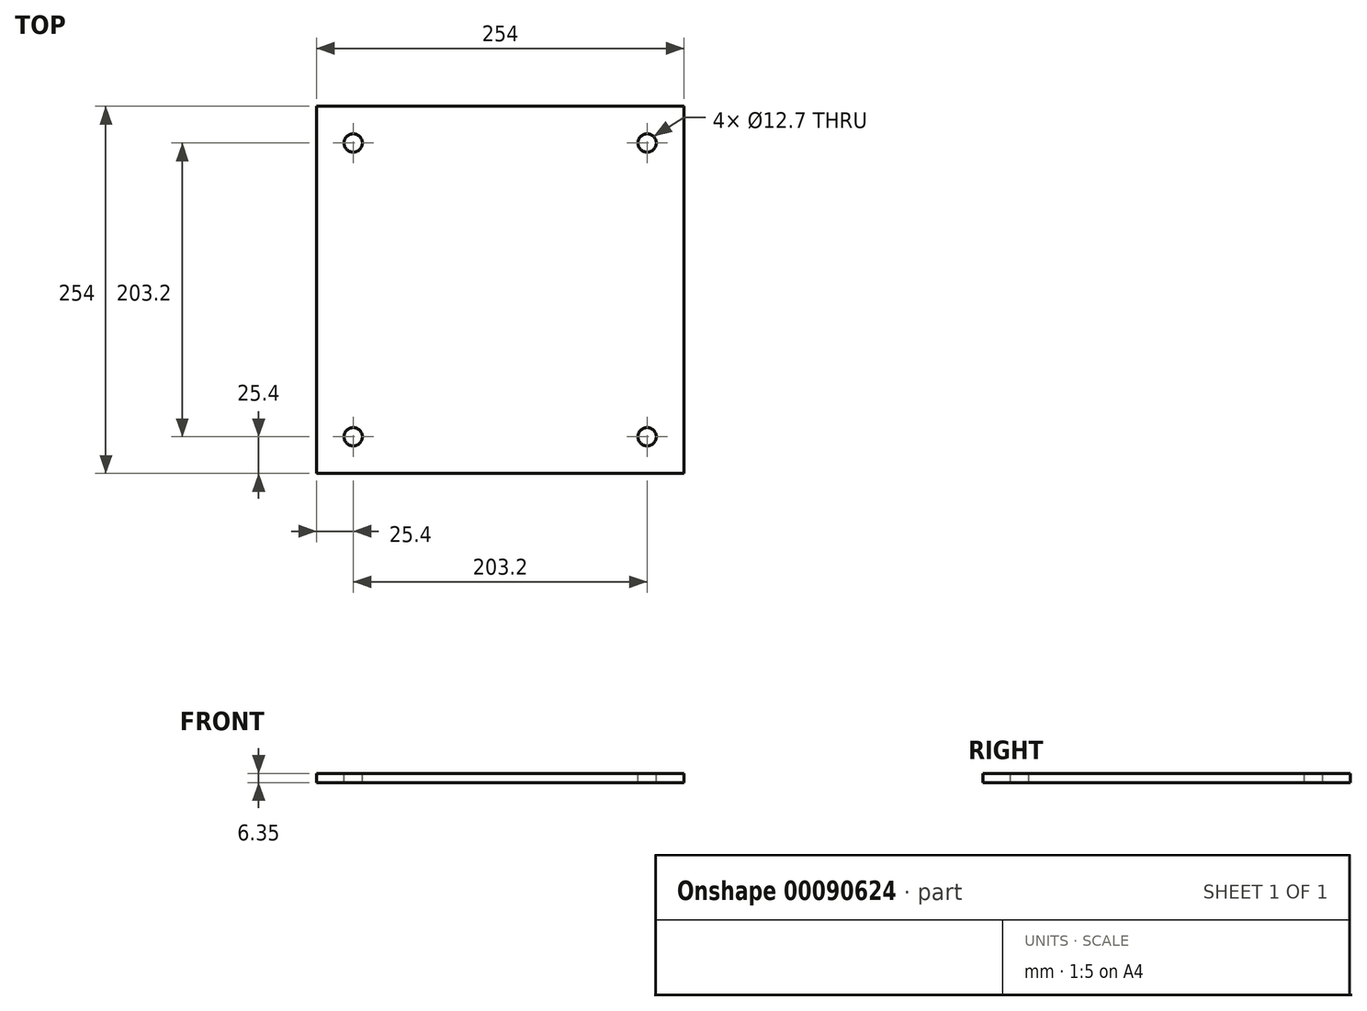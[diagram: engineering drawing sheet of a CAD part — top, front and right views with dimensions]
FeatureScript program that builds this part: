
annotation { "Feature Type Name" : "Feature", "Feature Type Description" : "" }
export const myFeature = defineFeature(function(context is Context, id is Id, definition is map)
    precondition{}
    {
        {
            var Q0;
            Q0=qCreatedBy(makeId("Top.planeOp"),FACE);
            var sketch = newSketch(context, id + "F0", { "sketchPlane" : qUnion([Q0])});
            skLineSegment(sketch, "E0.bottom", {"start": v(127, -127) * mm, "end": v(-127, -127) * mm});
            skLineSegment(sketch, "E0.top", {"start": v(127, 127) * mm, "end": v(-127, 127) * mm});
            skLineSegment(sketch, "E0.left", {"start": v(127, -127) * mm, "end": v(127, 127) * mm});
            skLineSegment(sketch, "E0.right", {"start": v(-127, -127) * mm, "end": v(-127, 127) * mm});
            skPoint(sketch, "E0.middle", {"position": v(0, 0) * mm});
            skSolve(sketch);
        }
        {
            var Q0;
            Q0 = qSketchRegion(id + "F0", true);
            extrude(context, id + "F1", {"entities" : qUnion([Q0]), "depth" : 6.35 * mm});
        }
        {
            var Q0;
            Q0=makeQuery(id+"F1.opExtrude","CAP_FACE",FACE,{"disambiguationData":[OSD([sQuery(id+"F0.wireOp",EDGE,"E0.bottom"),sQuery(id+"F0.wireOp",EDGE,"E0.top"),sQuery(id+"F0.wireOp",EDGE,"E0.left"),sQuery(id+"F0.wireOp",EDGE,"E0.right")])],"isStart":false});
            var sketch = newSketch(context, id + "F2", { "sketchPlane" : qUnion([Q0])});
            skCircle(sketch, "E1", {"center": v(-101.6, 101.6) * mm, "radius": 6.35 * mm});
            skCircle(sketch, "E2.0.1.0", {"center": v(-101.6, -101.6) * mm, "radius": 6.35 * mm});
            skCircle(sketch, "E2.1.0.0", {"center": v(101.6, 101.6) * mm, "radius": 6.35 * mm});
            skCircle(sketch, "E2.1.1.0", {"center": v(101.6, -101.6) * mm, "radius": 6.35 * mm});
            skLineSegment(sketch, "E2.direction1", {"start": v(-101.6, 101.6) * mm, "end": v(101.6, 101.6) * mm, "construction": true});
            skLineSegment(sketch, "E2.direction2", {"start": v(-101.6, 101.6) * mm, "end": v(-101.6, -101.6) * mm, "construction": true});
            skSolve(sketch);
        }
        {
            var Q0;
            Q0 = qSketchRegion(id + "F2", true);
            var Q1;
            {var subQ0=sQuery(id+"F2.wireOp",EDGE,"fcaae9ca-0fe3-4ba5-9361-49e8d2982260.0.left");var subQ5=sQuery(id+"F2.wireOp",EDGE,"fcaae9ca-0fe3-4ba5-9361-49e8d2982260.4.left");var subQ6=makeQuery(id+"F2.imprint","INTERSECT",VERTEX,{"derivedFrom":[subQ0,subQ5]});Q1=makeQuery(id+"F2.imprint","IMPRINT",FACE,{"disambiguationData":[TD([[makeQuery(id+"F2.imprint","IMPRINT",EDGE,{"disambiguationData":[TD([[subQ6,-1.0]])],"derivedFrom":subQ5}),-1.0]])]});}
            var Q2;
            {var subQ0=sQuery(id+"F2.wireOp",EDGE,"fcaae9ca-0fe3-4ba5-9361-49e8d2982260.3.right");var subQ5=sQuery(id+"F2.wireOp",EDGE,"fcaae9ca-0fe3-4ba5-9361-49e8d2982260.5.left");var subQ6=makeQuery(id+"F2.imprint","INTERSECT",VERTEX,{"derivedFrom":[subQ0,subQ5]});Q2=makeQuery(id+"F2.imprint","IMPRINT",FACE,{"disambiguationData":[TD([[makeQuery(id+"F2.imprint","IMPRINT",EDGE,{"disambiguationData":[TD([[subQ6,1.0]])],"derivedFrom":subQ5}),-1.0]])]});}
            var Q3;
            {var subQ3=sQuery(id+"F2.wireOp",EDGE,"fcaae9ca-0fe3-4ba5-9361-49e8d2982260.8.right");var subQ5=sQuery(id+"F2.wireOp",EDGE,"fcaae9ca-0fe3-4ba5-9361-49e8d2982260.0.left");var subQ6=makeQuery(id+"F2.imprint","INTERSECT",VERTEX,{"derivedFrom":[subQ5,subQ3]});Q3=makeQuery(id+"F2.imprint","IMPRINT",FACE,{"disambiguationData":[TD([[makeQuery(id+"F2.imprint","IMPRINT",EDGE,{"disambiguationData":[TD([[subQ6,-1.0]])],"derivedFrom":subQ5}),-1.0]])]});}
            var Q4;
            {var subQ3=sQuery(id+"F2.wireOp",EDGE,"fcaae9ca-0fe3-4ba5-9361-49e8d2982260.8.endCap");var subQ5=sQuery(id+"F2.wireOp",EDGE,"fcaae9ca-0fe3-4ba5-9361-49e8d2982260.6.right");var subQ6=makeQuery(id+"F2.imprint","INTERSECT",VERTEX,{"derivedFrom":[subQ5,subQ3]});Q4=makeQuery(id+"F2.imprint","IMPRINT",FACE,{"disambiguationData":[TD([[makeQuery(id+"F2.imprint","IMPRINT",EDGE,{"disambiguationData":[TD([[subQ6,-1.0]])],"derivedFrom":subQ5}),1.0]])]});}
            var Q5;
            {var subQ0=sQuery(id+"F2.wireOp",EDGE,"fcaae9ca-0fe3-4ba5-9361-49e8d2982260.6.startCap");Q5=makeQuery(id+"F2.imprint","IMPRINT",FACE,{"disambiguationData":[TD([[makeQuery(id+"F2.imprint","IMPRINT",EDGE,{"derivedFrom":subQ0}),1.0]])]});}
            var Q6;
            {var subQ4=sQuery(id+"F2.wireOp",EDGE,"fcaae9ca-0fe3-4ba5-9361-49e8d2982260.6.startCap");Q6=makeQuery(id+"F2.imprint","IMPRINT",FACE,{"disambiguationData":[TD([[makeQuery(id+"F2.imprint","IMPRINT",EDGE,{"derivedFrom":subQ4}),-1.0]])]});}
            var Q7;
            {var subQ0=sQuery(id+"F2.wireOp",EDGE,"fcaae9ca-0fe3-4ba5-9361-49e8d2982260.6.right");var subQ5=sQuery(id+"F2.wireOp",EDGE,"fcaae9ca-0fe3-4ba5-9361-49e8d2982260.3.right");var subQ7=makeQuery(id+"F2.imprint","INTERSECT",VERTEX,{"derivedFrom":[subQ5,subQ0]});Q7=makeQuery(id+"F2.imprint","IMPRINT",FACE,{"disambiguationData":[TD([[makeQuery(id+"F2.imprint","IMPRINT",EDGE,{"disambiguationData":[TD([[subQ7,-1.0]])],"derivedFrom":subQ5}),1.0]])]});}
            var Q8;
            {var subQ0=sQuery(id+"F2.wireOp",EDGE,"eogiIR2U-LT6g-LpLl-vn9w-FLxRaLRIBlY3");var subQ1=sQuery(id+"F2.wireOp",EDGE,"OlrpAAhb-PgXn-HwtC-GuVG-OjTCxttYwNpF");var subQ2=makeQuery(id+"F2.imprint","INTERSECT",VERTEX,{"derivedFrom":[subQ1,subQ0]});Q8=makeQuery(id+"F2.imprint","IMPRINT",FACE,{"disambiguationData":[TD([[makeQuery(id+"F2.imprint","IMPRINT",EDGE,{"disambiguationData":[TD([[subQ2,-1.0]])],"derivedFrom":subQ0}),-1.0]])]});}
            var Q9;
            {var subQ0=sQuery(id+"F2.wireOp",EDGE,"BpUyd5S9-NxuM-rI9K-ceQx-ny6DKXw1QPVt");var subQ1=sQuery(id+"F2.wireOp",EDGE,"OlrpAAhb-PgXn-HwtC-GuVG-OjTCxttYwNpF");var subQ2=makeQuery(id+"F2.imprint","INTERSECT",VERTEX,{"derivedFrom":[subQ1,subQ0]});Q9=makeQuery(id+"F2.imprint","IMPRINT",FACE,{"disambiguationData":[TD([[makeQuery(id+"F2.imprint","IMPRINT",EDGE,{"disambiguationData":[TD([[subQ2,1.0]])],"derivedFrom":subQ1}),1.0]])]});}
            var Q10;
            {var subQ0=sQuery(id+"F2.wireOp",EDGE,"UC7Wnhcp-SDgs-MwhC-QxEK-dL5DjtuIj0PG");var subQ1=sQuery(id+"F2.wireOp",EDGE,"RPupRvv0-u5yY-Xdj7-EinU-e93FE9O1bOhS");var subQ2=makeQuery(id+"F2.imprint","INTERSECT",VERTEX,{"derivedFrom":[subQ1,subQ0]});Q10=makeQuery(id+"F2.imprint","IMPRINT",FACE,{"disambiguationData":[TD([[makeQuery(id+"F2.imprint","IMPRINT",EDGE,{"disambiguationData":[TD([[subQ2,1.0]])],"derivedFrom":subQ1}),-1.0]])]});}
            var Q11;
            {var subQ0=sQuery(id+"F2.wireOp",EDGE,"UC7Wnhcp-SDgs-MwhC-QxEK-dL5DjtuIj0PG");var subQ1=sQuery(id+"F2.wireOp",EDGE,"skyEo2ta-Vul4-0HxA-M2Rf-Yz6B0rTyctfK");var subQ2=makeQuery(id+"F2.imprint","INTERSECT",VERTEX,{"derivedFrom":[subQ1,subQ0]});Q11=makeQuery(id+"F2.imprint","IMPRINT",FACE,{"disambiguationData":[TD([[makeQuery(id+"F2.imprint","IMPRINT",EDGE,{"disambiguationData":[TD([[subQ2,1.0]])],"derivedFrom":subQ0}),-1.0]])]});}
            var Q12;
            {var subQ0=sQuery(id+"F2.wireOp",EDGE,"skyEo2ta-Vul4-0HxA-M2Rf-Yz6B0rTyctfK");var subQ1=sQuery(id+"F2.wireOp",EDGE,"BpUyd5S9-NxuM-rI9K-ceQx-ny6DKXw1QPVt");var subQ2=makeQuery(id+"F2.imprint","INTERSECT",VERTEX,{"derivedFrom":[subQ1,subQ0]});Q12=makeQuery(id+"F2.imprint","IMPRINT",FACE,{"disambiguationData":[TD([[makeQuery(id+"F2.imprint","IMPRINT",EDGE,{"disambiguationData":[TD([[subQ2,1.0]])],"derivedFrom":subQ1}),1.0]])]});}
            extrude(context, id + "F3", {"entities" : qUnion([Q0, Q1, Q2, Q3, Q4, Q5, Q6, Q7, Q8, Q9, Q10, Q11, Q12]), "operationType" : NewBodyOperationType.REMOVE, "oppositeDirection" : true, "depth" : 12.7 * mm});
        }
        {
            var Q0;
            Q0 = qSketchRegion(id + "F2", true);
            extrude(context, id + "F4", {"entities" : qUnion([Q0]), "operationType" : NewBodyOperationType.REMOVE, "endBound" : BoundingType.THROUGH_ALL, "oppositeDirection" : true, "depth" : 25.4 * mm});
        }
    });
